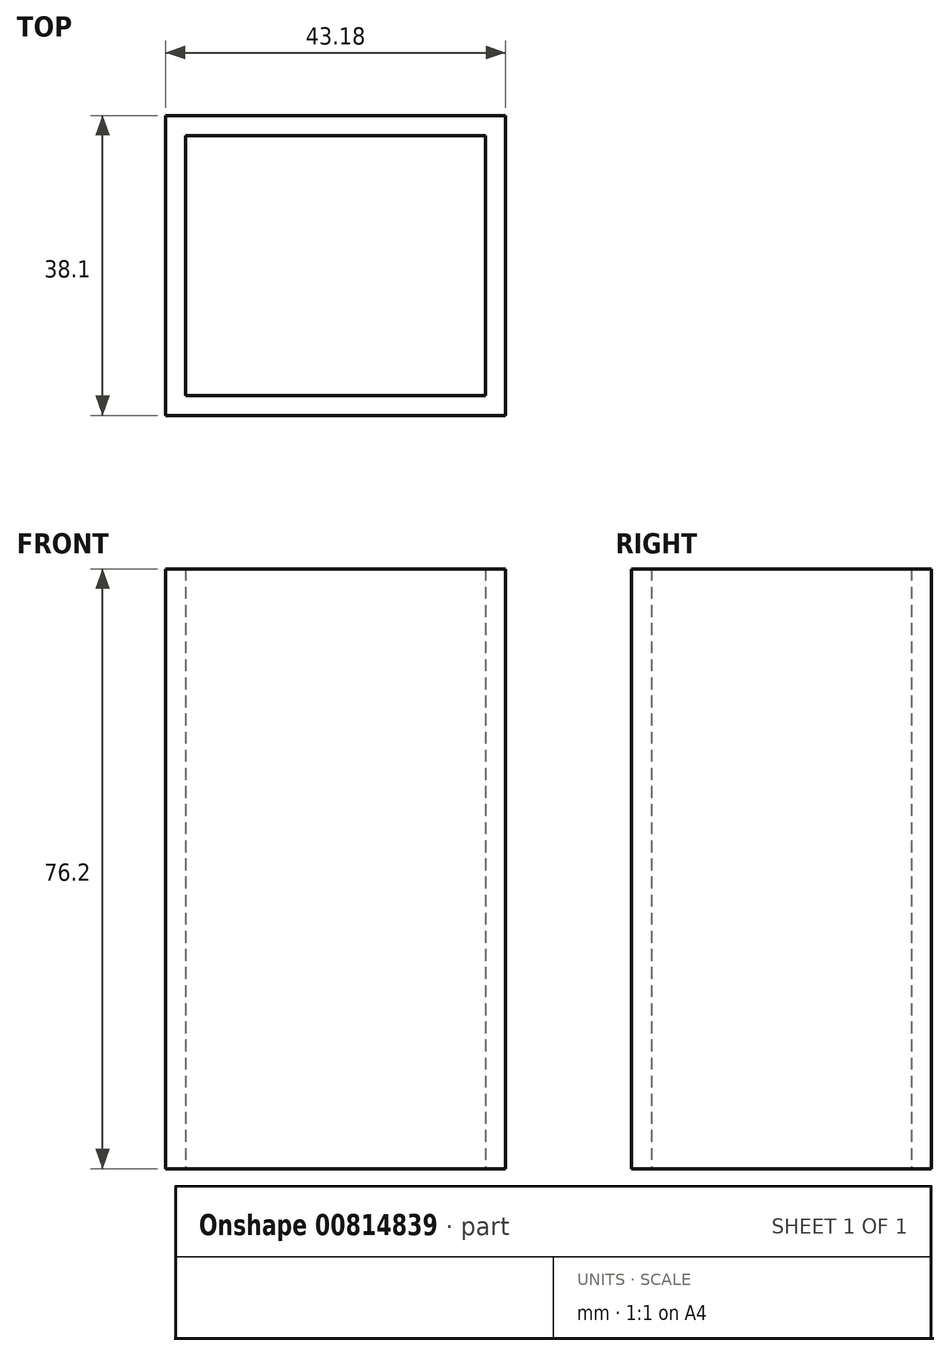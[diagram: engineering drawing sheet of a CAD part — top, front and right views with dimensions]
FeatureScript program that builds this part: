
annotation { "Feature Type Name" : "Feature", "Feature Type Description" : "" }
export const myFeature = defineFeature(function(context is Context, id is Id, definition is map)
    precondition{}
    {
        {
            var Q0;
            Q0=qCreatedBy(makeId("Top.planeOp"),FACE);
            var sketch = newSketch(context, id + "F0", { "sketchPlane" : qUnion([Q0])});
            skPoint(sketch, "E0.middle", {"position": v(0, 0) * mm});
            skCircle(sketch, "E1", {"center": v(-6.35, 0) * mm, "radius": 2.16 * mm, "construction": true});
            skCircle(sketch, "E2", {"center": v(6.35, 0) * mm, "radius": 2.16 * mm, "construction": true});
            skLineSegment(sketch, "E3.bottom", {"start": v(-21.59, 19.05) * mm, "end": v(21.6, 19.05) * mm});
            skLineSegment(sketch, "E3.top", {"start": v(-21.6, -19.05) * mm, "end": v(21.59, -19.05) * mm});
            skLineSegment(sketch, "E3.left", {"start": v(-21.59, 19.05) * mm, "end": v(-21.6, -19.05) * mm});
            skLineSegment(sketch, "E3.right", {"start": v(21.6, 19.05) * mm, "end": v(21.59, -19.05) * mm});
            skLineSegment(sketch, "E4.bottom", {"start": v(-19.05, 16.51) * mm, "end": v(19.05, 16.51) * mm});
            skLineSegment(sketch, "E4.top", {"start": v(-19.05, -16.51) * mm, "end": v(19.05, -16.51) * mm});
            skLineSegment(sketch, "E4.left", {"start": v(-19.05, 16.51) * mm, "end": v(-19.05, -16.51) * mm});
            skLineSegment(sketch, "E4.right", {"start": v(19.05, 16.51) * mm, "end": v(19.05, -16.51) * mm});
            skSolve(sketch);
        }
        {
            var Q0;
            Q0=makeQuery(id+"F0.imprint","IMPRINT",FACE,{"disambiguationData":[TD([[makeQuery(id+"F0.imprint","IMPRINT",EDGE,{"derivedFrom":sQuery(id+"F0.wireOp",EDGE,"E3.bottom")}),-1.0]])]});
            extrude(context, id + "F1", {"entities" : qUnion([Q0]), "endBound" : BoundingType.SYMMETRIC, "depth" : 76.2 * mm, "offsetDistance" : 25.4 * mm});
        }
    });
